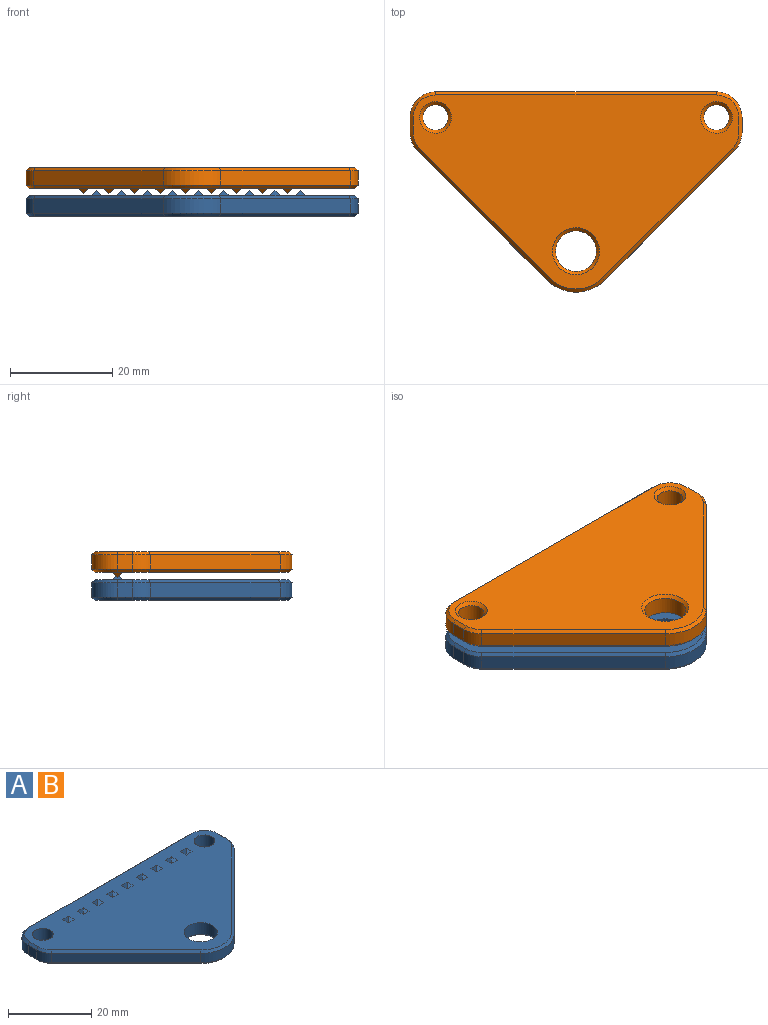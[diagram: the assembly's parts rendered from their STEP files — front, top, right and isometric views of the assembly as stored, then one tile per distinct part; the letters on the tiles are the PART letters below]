
ASSEMBLY  parts=2 mates=1
PART A: 74 faces, bbox 65x39.2x5 mm
  f0: plane 2x1mm, normal (0,-0.71,0.71), area 1.4mm2, adj f1,f3,f37
  f1: plane 2x1mm, normal (-0.71,0,0.71), area 1.4mm2, adj f0,f2,f37
  f2: plane 2x1mm, normal (0,0.71,0.71), area 1.4mm2, adj f1,f3,f37
  f3: plane 2x1mm, normal (0.71,0,0.71), area 1.4mm2, adj f0,f2,f37
  f4: plane 2x1mm, normal (0,-0.71,0.71), area 1.4mm2, adj f5,f7,f37
  f5: plane 2x1mm, normal (-0.71,0,0.71), area 1.4mm2, adj f4,f6,f37
  f6: plane 2x1mm, normal (0,0.71,0.71), area 1.4mm2, adj f5,f7,f37
  f7: plane 2x1mm, normal (0.71,0,0.71), area 1.4mm2, adj f4,f6,f37
  f8: plane 2x1mm, normal (0,-0.71,0.71), area 1.4mm2, adj f9,f11,f37
  f9: plane 2x1mm, normal (-0.71,0,0.71), area 1.4mm2, adj f8,f10,f37
  f10: plane 2x1mm, normal (0,0.71,0.71), area 1.4mm2, adj f9,f11,f37
  f11: plane 2x1mm, normal (0.71,0,0.71), area 1.4mm2, adj f8,f10,f37
  f12: plane 2x1mm, normal (0,-0.71,0.71), area 1.4mm2, adj f13,f15,f37
  f13: plane 2x1mm, normal (-0.71,0,0.71), area 1.4mm2, adj f12,f14,f37
  f14: plane 2x1mm, normal (0,0.71,0.71), area 1.4mm2, adj f13,f15,f37
  f15: plane 2x1mm, normal (0.71,0,0.71), area 1.4mm2, adj f12,f14,f37
  f16: plane 2x1mm, normal (0,-0.71,0.71), area 1.4mm2, adj f17,f19,f37
  f17: plane 2x1mm, normal (-0.71,0,0.71), area 1.4mm2, adj f16,f18,f37
  f18: plane 2x1mm, normal (0,0.71,0.71), area 1.4mm2, adj f17,f19,f37
  f19: plane 2x1mm, normal (0.71,0,0.71), area 1.4mm2, adj f16,f18,f37
  f20: plane 2x1mm, normal (0,-0.71,0.71), area 1.4mm2, adj f21,f23,f37
  f21: plane 2x1mm, normal (-0.71,0,0.71), area 1.4mm2, adj f20,f22,f37
  f22: plane 2x1mm, normal (0,0.71,0.71), area 1.4mm2, adj f21,f23,f37
  f23: plane 2x1mm, normal (0.71,0,0.71), area 1.4mm2, adj f20,f22,f37
  f24: plane 2x1mm, normal (0,-0.71,0.71), area 1.4mm2, adj f25,f27,f37
  f25: plane 2x1mm, normal (-0.71,0,0.71), area 1.4mm2, adj f24,f26,f37
  f26: plane 2x1mm, normal (0,0.71,0.71), area 1.4mm2, adj f25,f27,f37
  f27: plane 2x1mm, normal (0.71,0,0.71), area 1.4mm2, adj f24,f26,f37
  f28: plane 2x1mm, normal (0,-0.71,0.71), area 1.4mm2, adj f29,f31,f37
  f29: plane 2x1mm, normal (-0.71,0,0.71), area 1.4mm2, adj f28,f30,f37
  f30: plane 2x1mm, normal (0,0.71,0.71), area 1.4mm2, adj f29,f31,f37
  f31: plane 2x1mm, normal (0.71,0,0.71), area 1.4mm2, adj f28,f30,f37
  f32: plane 55x2.8mm, normal (0,1,0), area 154mm2, adj f49,f50,f59,f67
  f33: plane 2.93x2.8mm, normal (-1,0,0), area 8.2mm2, adj f40,f49,f55,f70
  f34: plane 25.38x25.38mm, normal (-0.71,-0.71,0), area 100.5mm2, adj f39,f40,f51,f66
  f35: plane 25.38x25.38mm, normal (0.71,-0.71,0), area 100.5mm2, adj f39,f41,f54,f62
  f36: plane 2.93x2.8mm, normal (1,0,0), area 8.2mm2, adj f41,f50,f58,f63
  f37: plane 63.8x37.99mm, normal (0,0,1), area 1455mm2, adj f0,f1,f2,f3,f4,f5,f6,f7
  f38: plane 63.8x37.99mm, normal (0,0,-1), area 1453.7mm2, adj f61,f62,f63,f64,f65,f66,f67,f68
  f39: cylinder r=8mm len=11.31mm, axis (0,0,-1), area 35.2mm2, adj f34,f35,f52,f64
  f40: cylinder r=5mm len=3.54mm, axis (0,0,-1), area 11mm2, adj f33,f34,f53,f68
  f41: cylinder r=5mm len=3.54mm, axis (0,0,-1), area 11mm2, adj f35,f36,f56,f61
  f42: cylinder r=2.5mm len=5mm, axis (0,0,1), area 53.4mm2, adj f37,f71
  f43: cylinder r=2.5mm len=5mm, axis (0,0,1), area 53.4mm2, adj f37,f72
  f44: cylinder r=4mm len=8mm, axis (0,0,1), area 85.5mm2, adj f37,f73
  f45: plane 2x1mm, normal (0.71,0,0.71), area 1.4mm2, adj f37,f46,f48
  f46: plane 2x1mm, normal (0,0.71,0.71), area 1.4mm2, adj f37,f45,f47
  f47: plane 2x1mm, normal (-0.71,0,0.71), area 1.4mm2, adj f37,f46,f48
  f48: plane 2x1mm, normal (0,-0.71,0.71), area 1.4mm2, adj f37,f45,f47
  f49: cylinder r=5mm len=5mm, axis (0,0,-1), area 22mm2, adj f32,f33,f57,f69
  f50: cylinder r=5mm len=5mm, axis (0,0,-1), area 22mm2, adj f32,f36,f60,f65
  f51: plane 25.8x25.8mm, normal (-0.5,-0.5,0.71), area 30.5mm2, adj f34,f37,f52,f53
  f52: cone r=7.4mm half-angle=45deg, axis (0,0,-1), area 10.3mm2, adj f37,f39,f51,f54
  f53: cone r=4.4mm half-angle=45deg, axis (0,0,-1), area 3.1mm2, adj f37,f40,f51,f55
  f54: plane 25.8x25.8mm, normal (0.5,-0.5,0.71), area 30.5mm2, adj f35,f37,f52,f56
  f55: plane 2.93x0.6mm, normal (-0.71,0,0.71), area 2.5mm2, adj f33,f37,f53,f57
  f56: cone r=4.4mm half-angle=45deg, axis (0,0,-1), area 3.1mm2, adj f37,f41,f54,f58
  f57: cone r=4.4mm half-angle=45deg, axis (0,0,-1), area 6.3mm2, adj f37,f49,f55,f59
  f58: plane 2.93x0.6mm, normal (0.71,0,0.71), area 2.5mm2, adj f36,f37,f56,f60
  f59: plane 55x0.6mm, normal (0,0.71,0.71), area 46.7mm2, adj f32,f37,f57,f60
  f60: cone r=4.4mm half-angle=45deg, axis (0,0,-1), area 6.3mm2, adj f37,f50,f58,f59
  f61: cone r=4.4mm half-angle=45deg, axis (0,0,1), area 3.1mm2, adj f38,f41,f62,f63
  f62: plane 25.8x25.8mm, normal (0.5,-0.5,-0.71), area 30.5mm2, adj f35,f38,f61,f64
  f63: plane 2.93x0.6mm, normal (0.71,0,-0.71), area 2.5mm2, adj f36,f38,f61,f65
  f64: cone r=7.4mm half-angle=45deg, axis (0,0,1), area 10.3mm2, adj f38,f39,f62,f66
  f65: cone r=4.4mm half-angle=45deg, axis (0,0,1), area 6.3mm2, adj f38,f50,f63,f67
  f66: plane 25.8x25.8mm, normal (-0.5,-0.5,-0.71), area 30.5mm2, adj f34,f38,f64,f68
  f67: plane 55x0.6mm, normal (0,0.71,-0.71), area 46.7mm2, adj f32,f38,f65,f69
  f68: cone r=4.4mm half-angle=45deg, axis (0,0,1), area 3.1mm2, adj f38,f40,f66,f70
  f69: cone r=4.4mm half-angle=45deg, axis (0,0,1), area 6.3mm2, adj f38,f49,f67,f70
  f70: plane 2.93x0.6mm, normal (-0.71,0,-0.71), area 2.5mm2, adj f33,f38,f68,f69
  f71: cone r=3.1mm half-angle=45deg, axis (0,0,-1), area 14.9mm2, adj f38,f42
  f72: cone r=3.1mm half-angle=45deg, axis (0,0,-1), area 14.9mm2, adj f38,f43
  f73: cone r=4.6mm half-angle=45deg, axis (0,0,-1), area 22.9mm2, adj f38,f44
PART B: same geometry as A
PLACE A at identity fixed
PLACE B rot(axis=(0,1,0),180deg) t=(0,0,9.5)mm
MATE fastened B.f43 <-> A.f42  axis (0,0,-1) through (-27.5,-5,5.5)mm
